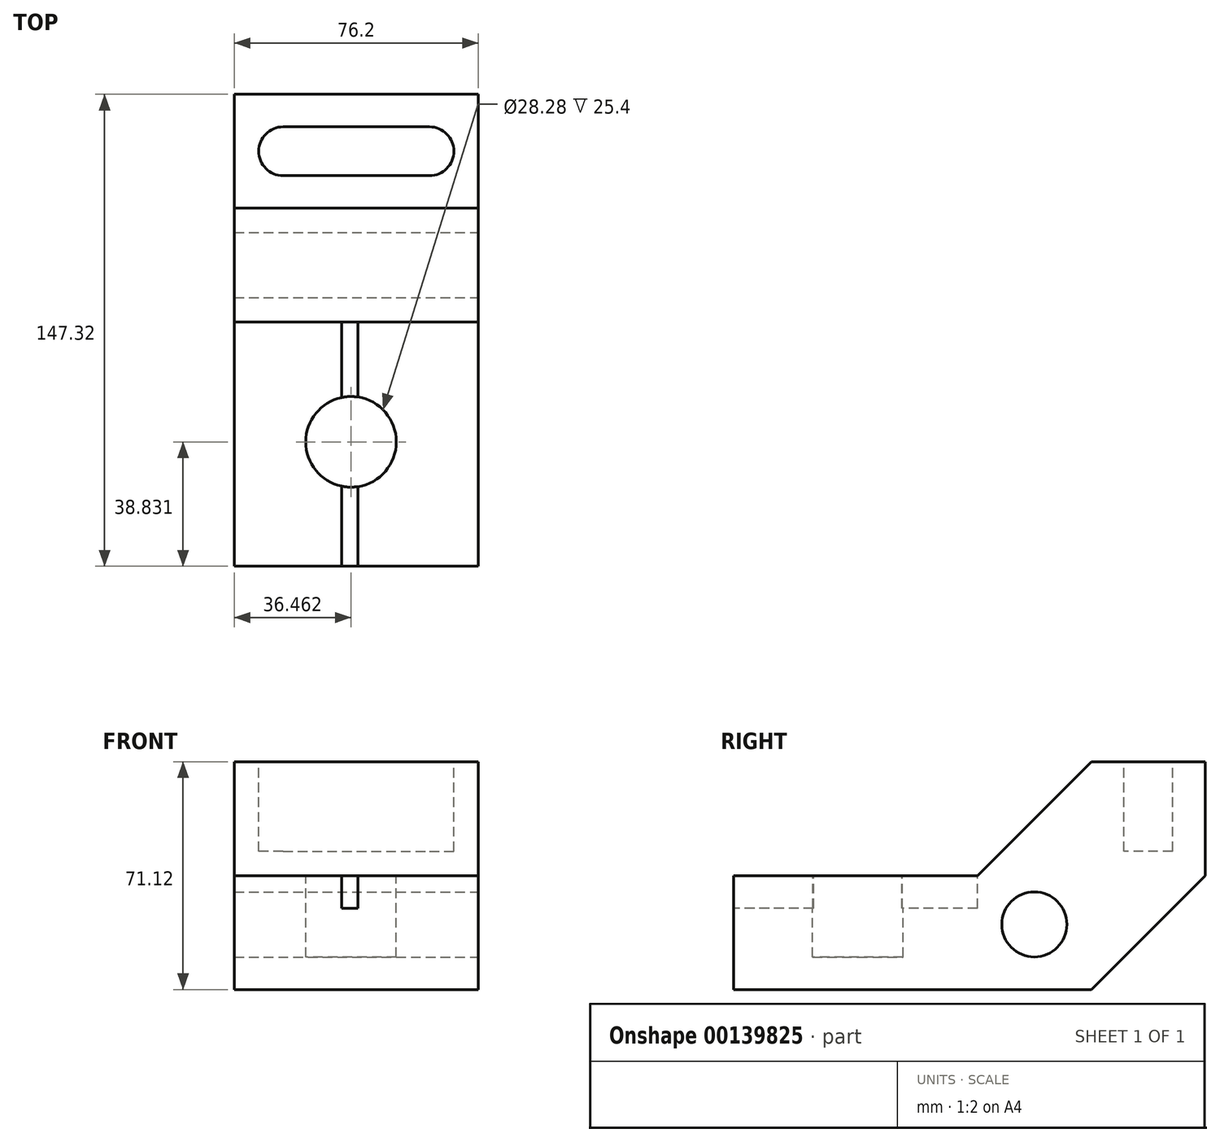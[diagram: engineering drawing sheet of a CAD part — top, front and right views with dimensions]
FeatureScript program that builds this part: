
annotation { "Feature Type Name" : "Feature", "Feature Type Description" : "" }
export const myFeature = defineFeature(function(context is Context, id is Id, definition is map)
    precondition{}
    {
        {
            var Q0;
            Q0=qCreatedBy(makeId("Right.planeOp"),FACE);
            var sketch = newSketch(context, id + "F0", { "sketchPlane" : qUnion([Q0])});
            skLineSegment(sketch, "E0", {"start": v(-76.2, 0) * mm, "end": v(35.56, 0) * mm});
            skLineSegment(sketch, "E1", {"start": v(35.56, 0) * mm, "end": v(71.12, 35.56) * mm});
            skLineSegment(sketch, "E2", {"start": v(71.12, 35.56) * mm, "end": v(71.12, 71.12) * mm});
            skLineSegment(sketch, "E3", {"start": v(71.12, 71.12) * mm, "end": v(35.56, 71.12) * mm});
            skLineSegment(sketch, "E4", {"start": v(35.56, 71.12) * mm, "end": v(0, 35.56) * mm});
            skLineSegment(sketch, "E5", {"start": v(0, 35.56) * mm, "end": v(-76.2, 35.56) * mm});
            skLineSegment(sketch, "E6", {"start": v(-76.2, 35.56) * mm, "end": v(-76.2, 0) * mm});
            skSolve(sketch);
        }
        {
            var Q0;
            Q0 = qSketchRegion(id + "F0", true);
            extrude(context, id + "F1", {"entities" : qUnion([Q0]), "depth" : 76.2 * mm});
        }
        {
            var Q0;
            Q0=makeQuery(id+"F1.opExtrude","SWEPT_FACE",FACE,{"disambiguationData":[OSD([sQuery(id+"F0.wireOp",EDGE,"E3")])]});
            var sketch = newSketch(context, id + "F2", { "sketchPlane" : qUnion([Q0])});
            skLineSegment(sketch, "E7", {"start": v(15.24, 60.96) * mm, "end": v(60.96, 60.96) * mm});
            skLineSegment(sketch, "E8", {"start": v(15.24, 45.72) * mm, "end": v(60.96, 45.72) * mm});
            skArc(sketch, "E9", {"start": v(15.24, 60.96) * mm, "mid": v(7.62, 53.34) * mm, "end": v(15.24, 45.72) * mm});
            skArc(sketch, "E10", {"start": v(60.96, 45.72) * mm, "mid": v(68.58, 53.34) * mm, "end": v(60.96, 60.96) * mm});
            skSolve(sketch);
        }
        {
            var Q0;
            Q0 = qSketchRegion(id + "F2", true);
            extrude(context, id + "F3", {"entities" : qUnion([Q0]), "operationType" : NewBodyOperationType.REMOVE, "oppositeDirection" : true, "depth" : 27.94 * mm});
        }
        {
            var Q0;
            Q0=makeQuery(id+"F1.opExtrude","CAP_FACE",FACE,{"disambiguationData":[OSD([sQuery(id+"F0.wireOp",EDGE,"E0"),sQuery(id+"F0.wireOp",EDGE,"E1"),sQuery(id+"F0.wireOp",EDGE,"E2"),sQuery(id+"F0.wireOp",EDGE,"E3"),sQuery(id+"F0.wireOp",EDGE,"E4"),sQuery(id+"F0.wireOp",EDGE,"E5"),sQuery(id+"F0.wireOp",EDGE,"E6")])],"isStart":false});
            var sketch = newSketch(context, id + "F4", { "sketchPlane" : qUnion([Q0])});
            skCircle(sketch, "E11", {"center": v(17.78, 20.32) * mm, "radius": 10.16 * mm});
            skSolve(sketch);
        }
        {
            var Q0;
            Q0 = qSketchRegion(id + "F4", true);
            extrude(context, id + "F5", {"entities" : qUnion([Q0]), "operationType" : NewBodyOperationType.REMOVE, "endBound" : BoundingType.THROUGH_ALL, "oppositeDirection" : true, "depth" : 25.4 * mm});
        }
        {
            var Q0;
            Q0=makeQuery(id+"F1.opExtrude","SWEPT_FACE",FACE,{"disambiguationData":[OSD([sQuery(id+"F0.wireOp",EDGE,"E5")])]});
            var sketch = newSketch(context, id + "F6", { "sketchPlane" : qUnion([Q0])});
            skLineSegment(sketch, "E12", {"start": v(33.51, 0) * mm, "end": v(33.51, -76.2) * mm});
            skLineSegment(sketch, "E13", {"start": v(38.6, 0) * mm, "end": v(38.6, -76.2) * mm});
            skLineSegment(sketch, "E14", {"start": v(33.51, 0) * mm, "end": v(38.6, 0) * mm});
            skLineSegment(sketch, "E15", {"start": v(33.51, -76.2) * mm, "end": v(38.6, -76.2) * mm});
            skPoint(sketch, "E16", {"position": v(36.23, -35.71) * mm});
            skSolve(sketch);
        }
        {
            var Q0;
            Q0 = qSketchRegion(id + "F6", true);
            extrude(context, id + "F7", {"entities" : qUnion([Q0]), "operationType" : NewBodyOperationType.REMOVE, "oppositeDirection" : true, "depth" : 10.16 * mm});
        }
        {
            var Q0;
            {var subQ2=sQuery(id+"F0.wireOp",EDGE,"E5");Q0=makeQuery(id+"F7.boolean.opBoolean","SPLIT",FACE,{"disambiguationData":[TD([makeQuery(id+"F7.opExtrude","SWEPT_FACE",FACE,{"disambiguationData":[OSD([sQuery(id+"F6.wireOp",EDGE,"E13")])]})])],"derivedFrom":makeQuery(id+"F1.opExtrude","SWEPT_FACE",FACE,{"disambiguationData":[OSD([subQ2])]})});}
            var sketch = newSketch(context, id + "F8", { "sketchPlane" : qUnion([Q0])});
            skCircle(sketch, "E17", {"center": v(36.46, -37.37) * mm, "radius": 14.14 * mm});
            skSolve(sketch);
        }
        {
            var Q0;
            Q0 = qSketchRegion(id + "F8", true);
            extrude(context, id + "F9", {"entities" : qUnion([Q0]), "operationType" : NewBodyOperationType.REMOVE, "oppositeDirection" : true, "depth" : 25.4 * mm});
        }
    });
